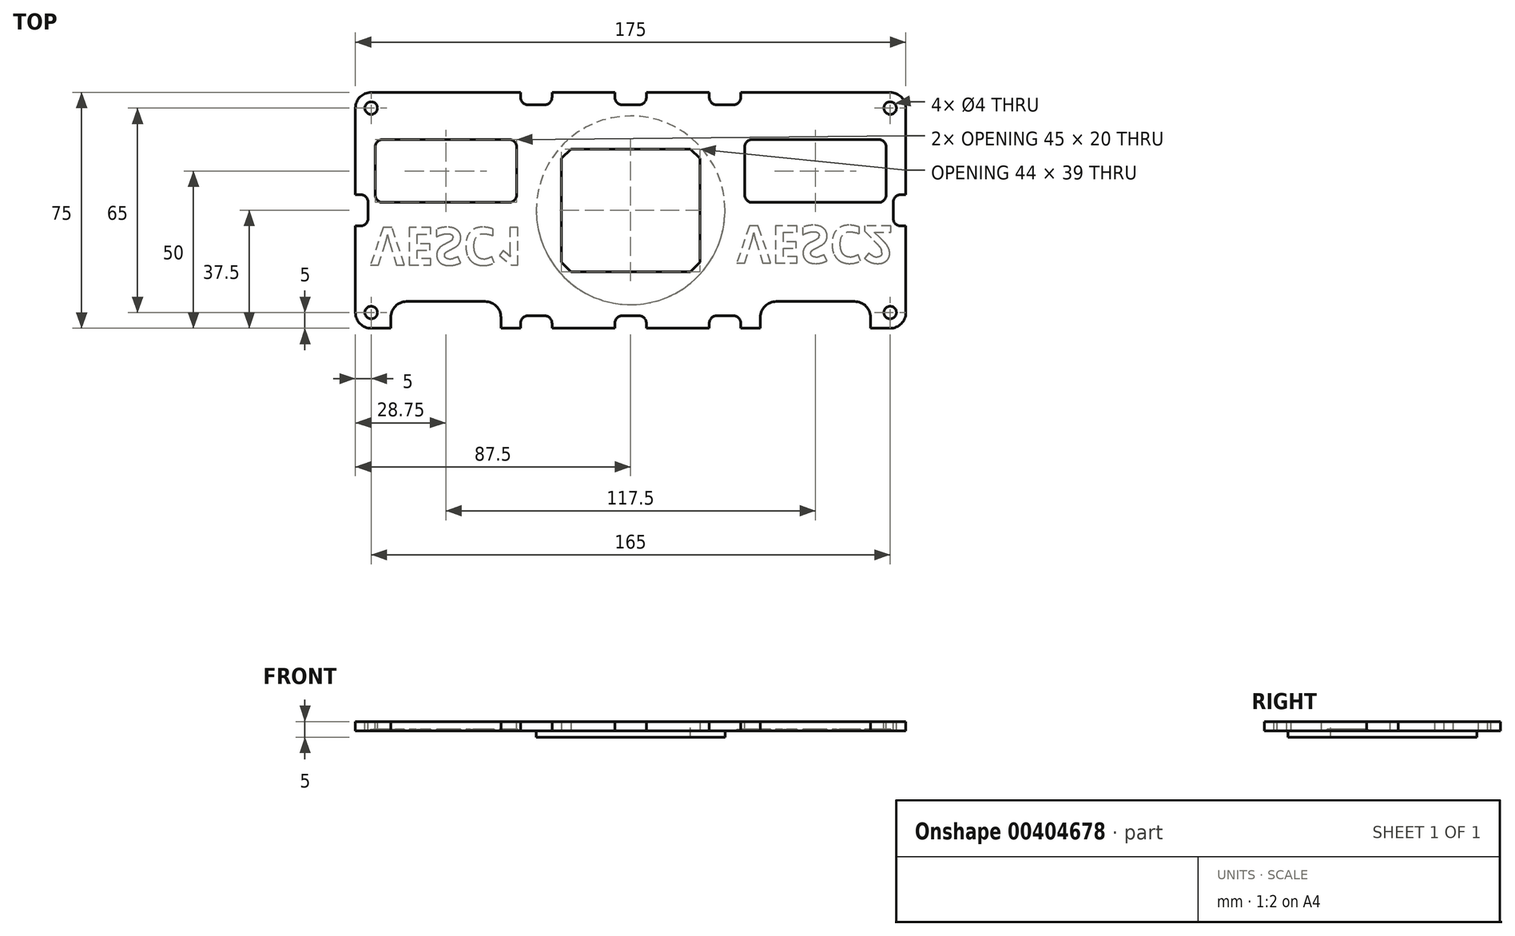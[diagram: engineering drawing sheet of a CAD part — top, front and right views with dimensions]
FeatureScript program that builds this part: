
annotation { "Feature Type Name" : "Feature", "Feature Type Description" : "" }
export const myFeature = defineFeature(function(context is Context, id is Id, definition is map)
    precondition{}
    {
        {
            var Q0;
            Q0=qCreatedBy(makeId("Top.planeOp"),FACE);
            var sketch = newSketch(context, id + "F0", { "sketchPlane" : qUnion([Q0])});
            skLineSegment(sketch, "E0.bottom", {"start": v(82.5, 37.5) * mm, "end": v(-82.5, 37.5) * mm});
            skLineSegment(sketch, "E0.top", {"start": v(82.5, -37.5) * mm, "end": v(-82.5, -37.5) * mm});
            skLineSegment(sketch, "E0.left", {"start": v(87.5, 32.5) * mm, "end": v(87.5, -32.5) * mm});
            skLineSegment(sketch, "E0.right", {"start": v(-87.5, 32.5) * mm, "end": v(-87.5, -32.5) * mm});
            skPoint(sketch, "E0.middle", {"position": v(0, 0) * mm});
            skPoint(sketch, "E1.visualSharp", {"position": v(-87.5, 37.5) * mm});
            skArc(sketch, "E1.filletArc", {"start": v(-82.5, 37.5) * mm, "mid": v(-86.04, 36.04) * mm, "end": v(-87.5, 32.5) * mm});
            skPoint(sketch, "E2.visualSharp", {"position": v(87.5, 37.5) * mm});
            skArc(sketch, "E2.filletArc", {"start": v(87.5, 32.5) * mm, "mid": v(86.04, 36.04) * mm, "end": v(82.5, 37.5) * mm});
            skPoint(sketch, "E3.visualSharp", {"position": v(87.5, -37.5) * mm});
            skArc(sketch, "E3.filletArc", {"start": v(82.5, -37.5) * mm, "mid": v(86.04, -36.04) * mm, "end": v(87.5, -32.5) * mm});
            skPoint(sketch, "E4.visualSharp", {"position": v(-87.5, -37.5) * mm});
            skArc(sketch, "E4.filletArc", {"start": v(-87.5, -32.5) * mm, "mid": v(-86.04, -36.04) * mm, "end": v(-82.5, -37.5) * mm});
            skSolve(sketch);
        }
        {
            var Q0;
            Q0=makeQuery(id+"F0.imprint","IMPRINT",FACE,{"disambiguationData":[TD([[makeQuery(id+"F0.imprint","IMPRINT",EDGE,{"derivedFrom":sQuery(id+"F0.wireOp",EDGE,"E0.bottom")}),1.0]])]});
            extrude(context, id + "F1", {"entities" : qUnion([Q0]), "depth" : 3 * mm});
        }
        {
            var Q0;
            Q0=makeQuery(id+"F1.opExtrude","CAP_FACE",FACE,{"disambiguationData":[OSD([sQuery(id+"F0.wireOp",EDGE,"E0.bottom"),sQuery(id+"F0.wireOp",EDGE,"E0.top"),sQuery(id+"F0.wireOp",EDGE,"E0.left"),sQuery(id+"F0.wireOp",EDGE,"E0.right"),sQuery(id+"F0.wireOp",EDGE,"E1.filletArc"),sQuery(id+"F0.wireOp",EDGE,"E2.filletArc"),sQuery(id+"F0.wireOp",EDGE,"E3.filletArc"),sQuery(id+"F0.wireOp",EDGE,"E4.filletArc")])],"isStart":false});
            var sketch = newSketch(context, id + "F2", { "sketchPlane" : qUnion([Q0])});
            skLineSegment(sketch, "E5.bottom", {"start": v(35, 41.5) * mm, "end": v(-35, 41.5) * mm});
            skLineSegment(sketch, "E5.top", {"start": v(35, 33.5) * mm, "end": v(-35, 33.5) * mm});
            skLineSegment(sketch, "E5.left", {"start": v(35, 41.5) * mm, "end": v(35, 33.5) * mm});
            skLineSegment(sketch, "E5.right", {"start": v(-35, 41.5) * mm, "end": v(-35, 33.5) * mm});
            skPoint(sketch, "E5.middle", {"position": v(0, 37.5) * mm});
            skLineSegment(sketch, "E6.bottom", {"start": v(35, -41.5) * mm, "end": v(-35, -41.5) * mm});
            skLineSegment(sketch, "E6.top", {"start": v(35, -33.5) * mm, "end": v(-35, -33.5) * mm});
            skLineSegment(sketch, "E6.left", {"start": v(35, -41.5) * mm, "end": v(35, -33.5) * mm});
            skLineSegment(sketch, "E6.right", {"start": v(-35, -41.5) * mm, "end": v(-35, -33.5) * mm});
            skPoint(sketch, "E6.middle", {"position": v(0, -37.5) * mm});
            skLineSegment(sketch, "E7.bottom", {"start": v(-91.5, -5) * mm, "end": v(-83.5, -5) * mm});
            skLineSegment(sketch, "E7.top", {"start": v(-91.5, 5) * mm, "end": v(-83.5, 5) * mm});
            skLineSegment(sketch, "E7.left", {"start": v(-91.5, -5) * mm, "end": v(-91.5, 5) * mm});
            skLineSegment(sketch, "E7.right", {"start": v(-83.5, -5) * mm, "end": v(-83.5, 5) * mm});
            skPoint(sketch, "E7.middle", {"position": v(-87.5, 0) * mm});
            skLineSegment(sketch, "E8.bottom", {"start": v(91.5, -5) * mm, "end": v(83.5, -5) * mm});
            skLineSegment(sketch, "E8.top", {"start": v(91.5, 5) * mm, "end": v(83.5, 5) * mm});
            skLineSegment(sketch, "E8.left", {"start": v(91.5, -5) * mm, "end": v(91.5, 5) * mm});
            skLineSegment(sketch, "E8.right", {"start": v(83.5, -5) * mm, "end": v(83.5, 5) * mm});
            skPoint(sketch, "E8.middle", {"position": v(87.5, 0) * mm});
            skSolve(sketch);
        }
        {
            var Q0;
            {var subQ0=sQuery(id+"F2.wireOp",EDGE,"E7.right");Q0=makeQuery(id+"F2.imprint","IMPRINT",FACE,{"disambiguationData":[TD([[makeQuery(id+"F2.imprint","IMPRINT",EDGE,{"derivedFrom":subQ0}),1.0]])]});}
            var Q1;
            {var subQ0=sQuery(id+"F2.wireOp",EDGE,"E7.left");Q1=makeQuery(id+"F2.imprint","IMPRINT",FACE,{"disambiguationData":[TD([[makeQuery(id+"F2.imprint","IMPRINT",EDGE,{"derivedFrom":subQ0}),-1.0]])]});}
            var Q2;
            {var subQ0=sQuery(id+"F2.wireOp",EDGE,"E5.top");Q2=makeQuery(id+"F2.imprint","IMPRINT",FACE,{"disambiguationData":[TD([[makeQuery(id+"F2.imprint","IMPRINT",EDGE,{"derivedFrom":subQ0}),-1.0]])]});}
            var Q3;
            {var subQ0=sQuery(id+"F2.wireOp",EDGE,"E5.bottom");Q3=makeQuery(id+"F2.imprint","IMPRINT",FACE,{"disambiguationData":[TD([[makeQuery(id+"F2.imprint","IMPRINT",EDGE,{"derivedFrom":subQ0}),1.0]])]});}
            var Q4;
            {var subQ0=sQuery(id+"F2.wireOp",EDGE,"E8.right");Q4=makeQuery(id+"F2.imprint","IMPRINT",FACE,{"disambiguationData":[TD([[makeQuery(id+"F2.imprint","IMPRINT",EDGE,{"derivedFrom":subQ0}),-1.0]])]});}
            var Q5;
            {var subQ0=sQuery(id+"F2.wireOp",EDGE,"E8.left");Q5=makeQuery(id+"F2.imprint","IMPRINT",FACE,{"disambiguationData":[TD([[makeQuery(id+"F2.imprint","IMPRINT",EDGE,{"derivedFrom":subQ0}),1.0]])]});}
            var Q6;
            {var subQ0=sQuery(id+"F2.wireOp",EDGE,"E6.top");Q6=makeQuery(id+"F2.imprint","IMPRINT",FACE,{"disambiguationData":[TD([[makeQuery(id+"F2.imprint","IMPRINT",EDGE,{"derivedFrom":subQ0}),1.0]])]});}
            var Q7;
            {var subQ0=sQuery(id+"F2.wireOp",EDGE,"E6.bottom");Q7=makeQuery(id+"F2.imprint","IMPRINT",FACE,{"disambiguationData":[TD([[makeQuery(id+"F2.imprint","IMPRINT",EDGE,{"derivedFrom":subQ0}),-1.0]])]});}
            extrude(context, id + "F3", {"entities" : qUnion([Q0, Q1, Q2, Q3, Q4, Q5, Q6, Q7]), "operationType" : NewBodyOperationType.REMOVE, "oppositeDirection" : true, "depth" : 20.4 * mm});
        }
        {
            var Q0;
            Q0=makeQuery(id+"F1.opExtrude","CAP_FACE",FACE,{"disambiguationData":[OSD([sQuery(id+"F0.wireOp",EDGE,"E0.bottom"),sQuery(id+"F0.wireOp",EDGE,"E0.top"),sQuery(id+"F0.wireOp",EDGE,"E0.left"),sQuery(id+"F0.wireOp",EDGE,"E0.right"),sQuery(id+"F0.wireOp",EDGE,"E1.filletArc"),sQuery(id+"F0.wireOp",EDGE,"E2.filletArc"),sQuery(id+"F0.wireOp",EDGE,"E3.filletArc"),sQuery(id+"F0.wireOp",EDGE,"E4.filletArc")])],"isStart":false});
            var sketch = newSketch(context, id + "F4", { "sketchPlane" : qUnion([Q0])});
            skCircle(sketch, "E9", {"center": v(-82.5, 32.5) * mm, "radius": 2 * mm});
            skCircle(sketch, "E10", {"center": v(82.5, 32.5) * mm, "radius": 2 * mm});
            skCircle(sketch, "E11", {"center": v(-82.5, -32.5) * mm, "radius": 2 * mm});
            skCircle(sketch, "E12", {"center": v(82.5, -32.5) * mm, "radius": 2 * mm});
            skSolve(sketch);
        }
        {
            var Q0;
            Q0=makeQuery(id+"F4.imprint","IMPRINT",FACE,{"disambiguationData":[TD([[makeQuery(id+"F4.imprint","IMPRINT",EDGE,{"derivedFrom":sQuery(id+"F4.wireOp",EDGE,"E9")}),1.0]])]});
            var Q1;
            Q1=makeQuery(id+"F4.imprint","IMPRINT",FACE,{"disambiguationData":[TD([[makeQuery(id+"F4.imprint","IMPRINT",EDGE,{"derivedFrom":sQuery(id+"F4.wireOp",EDGE,"E11")}),1.0]])]});
            var Q2;
            Q2=makeQuery(id+"F4.imprint","IMPRINT",FACE,{"disambiguationData":[TD([[makeQuery(id+"F4.imprint","IMPRINT",EDGE,{"derivedFrom":sQuery(id+"F4.wireOp",EDGE,"E10")}),1.0]])]});
            var Q3;
            Q3=makeQuery(id+"F4.imprint","IMPRINT",FACE,{"disambiguationData":[TD([[makeQuery(id+"F4.imprint","IMPRINT",EDGE,{"derivedFrom":sQuery(id+"F4.wireOp",EDGE,"E12")}),1.0]])]});
            extrude(context, id + "F5", {"entities" : qUnion([Q0, Q1, Q2, Q3]), "operationType" : NewBodyOperationType.REMOVE, "oppositeDirection" : true, "depth" : 25 * mm});
        }
        {
            var Q0;
            Q0=makeQuery(id+"F1.opExtrude","CAP_FACE",FACE,{"disambiguationData":[OSD([sQuery(id+"F0.wireOp",EDGE,"E0.bottom"),sQuery(id+"F0.wireOp",EDGE,"E0.top"),sQuery(id+"F0.wireOp",EDGE,"E0.left"),sQuery(id+"F0.wireOp",EDGE,"E0.right"),sQuery(id+"F0.wireOp",EDGE,"E1.filletArc"),sQuery(id+"F0.wireOp",EDGE,"E2.filletArc"),sQuery(id+"F0.wireOp",EDGE,"E3.filletArc"),sQuery(id+"F0.wireOp",EDGE,"E4.filletArc")])],"isStart":false});
            var sketch = newSketch(context, id + "F6", { "sketchPlane" : qUnion([Q0])});
            skLineSegment(sketch, "E13.bottom", {"start": v(22, 19.5) * mm, "end": v(-22, 19.5) * mm});
            skLineSegment(sketch, "E13.top", {"start": v(22, -19.5) * mm, "end": v(-22, -19.5) * mm});
            skLineSegment(sketch, "E13.left", {"start": v(22, 19.5) * mm, "end": v(22, -19.5) * mm});
            skLineSegment(sketch, "E13.right", {"start": v(-22, 19.5) * mm, "end": v(-22, -19.5) * mm});
            skPoint(sketch, "E13.middle", {"position": v(0, 0) * mm});
            skSolve(sketch);
        }
        {
            var Q0;
            Q0=makeQuery(id+"F6.imprint","IMPRINT",FACE,{"disambiguationData":[TD([[makeQuery(id+"F6.imprint","IMPRINT",EDGE,{"derivedFrom":sQuery(id+"F6.wireOp",EDGE,"E13.bottom")}),1.0]])]});
            extrude(context, id + "F7", {"entities" : qUnion([Q0]), "operationType" : NewBodyOperationType.REMOVE, "oppositeDirection" : true, "depth" : 25 * mm});
        }
        {
            var Q0;
            Q0=makeQuery(id+"F1.opExtrude","CAP_FACE",FACE,{"disambiguationData":[OSD([sQuery(id+"F0.wireOp",EDGE,"E0.bottom"),sQuery(id+"F0.wireOp",EDGE,"E0.top"),sQuery(id+"F0.wireOp",EDGE,"E0.left"),sQuery(id+"F0.wireOp",EDGE,"E0.right"),sQuery(id+"F0.wireOp",EDGE,"E1.filletArc"),sQuery(id+"F0.wireOp",EDGE,"E2.filletArc"),sQuery(id+"F0.wireOp",EDGE,"E3.filletArc"),sQuery(id+"F0.wireOp",EDGE,"E4.filletArc")])],"isStart":false});
            var sketch = newSketch(context, id + "F8", { "sketchPlane" : qUnion([Q0])});
            skLineSegment(sketch, "E14.bottom", {"start": v(-41.25, -46) * mm, "end": v(-76.25, -46) * mm});
            skLineSegment(sketch, "E14.top", {"start": v(-46.25, -29) * mm, "end": v(-71.25, -29) * mm});
            skLineSegment(sketch, "E14.left", {"start": v(-41.25, -46) * mm, "end": v(-41.25, -34) * mm});
            skLineSegment(sketch, "E14.right", {"start": v(-76.25, -46) * mm, "end": v(-76.25, -34) * mm});
            skPoint(sketch, "E14.middle", {"position": v(-58.75, -37.5) * mm});
            skPoint(sketch, "E15.visualSharp", {"position": v(-76.25, -29) * mm});
            skArc(sketch, "E15.filletArc", {"start": v(-71.25, -29) * mm, "mid": v(-74.79, -30.46) * mm, "end": v(-76.25, -34) * mm});
            skPoint(sketch, "E16.visualSharp", {"position": v(-41.25, -29) * mm});
            skArc(sketch, "E16.filletArc", {"start": v(-41.25, -34) * mm, "mid": v(-42.71, -30.46) * mm, "end": v(-46.25, -29) * mm});
            skLineSegment(sketch, "E17.bottom", {"start": v(76.25, -46) * mm, "end": v(41.25, -46) * mm});
            skLineSegment(sketch, "E17.top", {"start": v(71.25, -29) * mm, "end": v(46.25, -29) * mm});
            skLineSegment(sketch, "E17.left", {"start": v(76.25, -46) * mm, "end": v(76.25, -34) * mm});
            skLineSegment(sketch, "E17.right", {"start": v(41.25, -46) * mm, "end": v(41.25, -34) * mm});
            skPoint(sketch, "E17.middle", {"position": v(58.75, -37.5) * mm});
            skPoint(sketch, "E18.visualSharp", {"position": v(41.25, -29) * mm});
            skArc(sketch, "E18.filletArc", {"start": v(46.25, -29) * mm, "mid": v(42.71, -30.46) * mm, "end": v(41.25, -34) * mm});
            skPoint(sketch, "E19.visualSharp", {"position": v(76.25, -29) * mm});
            skArc(sketch, "E19.filletArc", {"start": v(76.25, -34) * mm, "mid": v(74.79, -30.46) * mm, "end": v(71.25, -29) * mm});
            skSolve(sketch);
        }
        {
            var Q0;
            Q0 = qSketchRegion(id + "F8", true);
            extrude(context, id + "F9", {"entities" : qUnion([Q0]), "operationType" : NewBodyOperationType.REMOVE, "oppositeDirection" : true, "depth" : 25 * mm});
        }
        {
            var Q0;
            Q0=makeQuery(id+"F1.opExtrude","CAP_FACE",FACE,{"disambiguationData":[OSD([sQuery(id+"F0.wireOp",EDGE,"E0.bottom"),sQuery(id+"F0.wireOp",EDGE,"E0.top"),sQuery(id+"F0.wireOp",EDGE,"E0.left"),sQuery(id+"F0.wireOp",EDGE,"E0.right"),sQuery(id+"F0.wireOp",EDGE,"E1.filletArc"),sQuery(id+"F0.wireOp",EDGE,"E2.filletArc"),sQuery(id+"F0.wireOp",EDGE,"E3.filletArc"),sQuery(id+"F0.wireOp",EDGE,"E4.filletArc")])],"isStart":false});
            var sketch = newSketch(context, id + "F10", { "sketchPlane" : qUnion([Q0])});
            skLineSegment(sketch, "E20.bottom", {"start": v(5, -37.5) * mm, "end": v(-5, -37.5) * mm});
            skLineSegment(sketch, "E20.top", {"start": v(5, -29.5) * mm, "end": v(-5, -29.5) * mm});
            skLineSegment(sketch, "E20.left", {"start": v(5, -37.5) * mm, "end": v(5, -29.5) * mm});
            skLineSegment(sketch, "E20.right", {"start": v(-5, -37.5) * mm, "end": v(-5, -29.5) * mm});
            skPoint(sketch, "E20.middle", {"position": v(0, -33.5) * mm});
            skLineSegment(sketch, "E21.bottom", {"start": v(-5, -37.5) * mm, "end": v(-25, -37.5) * mm});
            skLineSegment(sketch, "E21.top", {"start": v(-5, -29.5) * mm, "end": v(-25, -29.5) * mm});
            skLineSegment(sketch, "E21.right", {"start": v(-25, -37.5) * mm, "end": v(-25, -29.5) * mm});
            skPoint(sketch, "E21.middle", {"position": v(-15, -33.5) * mm});
            skLineSegment(sketch, "E22.bottom", {"start": v(5, -37.5) * mm, "end": v(25, -37.5) * mm});
            skLineSegment(sketch, "E22.top", {"start": v(5, -29.5) * mm, "end": v(25, -29.5) * mm});
            skLineSegment(sketch, "E22.right", {"start": v(25, -37.5) * mm, "end": v(25, -29.5) * mm});
            skPoint(sketch, "E22.middle", {"position": v(15, -33.5) * mm});
            skLineSegment(sketch, "E23", {"start": v(-98.16, 0) * mm, "end": v(103.56, 0) * mm});
            skLineSegment(sketch, "E24.MirrorCS", {"start": v(-5, 37.5) * mm, "end": v(-25, 37.5) * mm});
            skLineSegment(sketch, "E25.MirrorCS", {"start": v(-25, 37.5) * mm, "end": v(-25, 29.5) * mm});
            skLineSegment(sketch, "E26.MirrorCS", {"start": v(-5, 29.5) * mm, "end": v(-25, 29.5) * mm});
            skLineSegment(sketch, "E27.MirrorCS", {"start": v(-5, 37.5) * mm, "end": v(-5, 29.5) * mm});
            skLineSegment(sketch, "E28.MirrorCS", {"start": v(5, 37.5) * mm, "end": v(5, 29.5) * mm});
            skLineSegment(sketch, "E29.MirrorCS", {"start": v(5, 29.5) * mm, "end": v(25, 29.5) * mm});
            skLineSegment(sketch, "E30.MirrorCS", {"start": v(5, 37.5) * mm, "end": v(25, 37.5) * mm});
            skLineSegment(sketch, "E31.MirrorCS", {"start": v(25, 37.5) * mm, "end": v(25, 29.5) * mm});
            skSolve(sketch);
        }
        {
            var Q0;
            {var subQ0=sQuery(id+"F10.wireOp",EDGE,"E21.bottom");Q0=makeQuery(id+"F10.imprint","IMPRINT",FACE,{"disambiguationData":[TD([[makeQuery(id+"F10.imprint","IMPRINT",EDGE,{"derivedFrom":subQ0}),-1.0]])]});}
            var Q1;
            {var subQ0=sQuery(id+"F10.wireOp",EDGE,"E22.bottom");Q1=makeQuery(id+"F10.imprint","IMPRINT",FACE,{"disambiguationData":[TD([[makeQuery(id+"F10.imprint","IMPRINT",EDGE,{"derivedFrom":subQ0}),1.0]])]});}
            var Q2;
            {var subQ0=sQuery(id+"F10.wireOp",EDGE,"E21.top");Q2=makeQuery(id+"F10.imprint","IMPRINT",FACE,{"disambiguationData":[TD([[makeQuery(id+"F10.imprint","IMPRINT",EDGE,{"derivedFrom":subQ0}),1.0]])]});}
            var Q3;
            {var subQ0=sQuery(id+"F10.wireOp",EDGE,"E22.top");Q3=makeQuery(id+"F10.imprint","IMPRINT",FACE,{"disambiguationData":[TD([[makeQuery(id+"F10.imprint","IMPRINT",EDGE,{"derivedFrom":subQ0}),-1.0]])]});}
            var Q4;
            {var subQ0=sQuery(id+"F10.wireOp",EDGE,"E26.MirrorCS");Q4=makeQuery(id+"F10.imprint","IMPRINT",FACE,{"disambiguationData":[TD([[makeQuery(id+"F10.imprint","IMPRINT",EDGE,{"derivedFrom":subQ0}),-1.0]])]});}
            var Q5;
            {var subQ0=sQuery(id+"F10.wireOp",EDGE,"E24.MirrorCS");Q5=makeQuery(id+"F10.imprint","IMPRINT",FACE,{"disambiguationData":[TD([[makeQuery(id+"F10.imprint","IMPRINT",EDGE,{"derivedFrom":subQ0}),1.0]])]});}
            var Q6;
            {var subQ0=sQuery(id+"F10.wireOp",EDGE,"E30.MirrorCS");Q6=makeQuery(id+"F10.imprint","IMPRINT",FACE,{"disambiguationData":[TD([[makeQuery(id+"F10.imprint","IMPRINT",EDGE,{"derivedFrom":subQ0}),-1.0]])]});}
            var Q7;
            {var subQ0=sQuery(id+"F10.wireOp",EDGE,"E29.MirrorCS");Q7=makeQuery(id+"F10.imprint","IMPRINT",FACE,{"disambiguationData":[TD([[makeQuery(id+"F10.imprint","IMPRINT",EDGE,{"derivedFrom":subQ0}),1.0]])]});}
            extrude(context, id + "F11", {"entities" : qUnion([Q0, Q1, Q2, Q3, Q4, Q5, Q6, Q7]), "operationType" : NewBodyOperationType.ADD, "oppositeDirection" : true, "depth" : 3 * mm});
        }
        {
            var Q0;
            Q0=makeQuery(id+"F11.boolean.opBoolean","MERGE",FACE,{"derivedFrom":[makeQuery(id+"F1.opExtrude","CAP_FACE",FACE,{"disambiguationData":[OSD([sQuery(id+"F0.wireOp",EDGE,"E0.bottom"),sQuery(id+"F0.wireOp",EDGE,"E0.top"),sQuery(id+"F0.wireOp",EDGE,"E0.left"),sQuery(id+"F0.wireOp",EDGE,"E0.right"),sQuery(id+"F0.wireOp",EDGE,"E1.filletArc"),sQuery(id+"F0.wireOp",EDGE,"E2.filletArc"),sQuery(id+"F0.wireOp",EDGE,"E3.filletArc"),sQuery(id+"F0.wireOp",EDGE,"E4.filletArc")])],"isStart":false}),makeQuery(id+"F11.opExtrude","CAP_FACE",FACE,{"disambiguationData":[OSD([sQuery(id+"F10.wireOp",EDGE,"E21.bottom"),sQuery(id+"F10.wireOp",EDGE,"E21.top"),sQuery(id+"F10.wireOp",EDGE,"E20.right"),sQuery(id+"F10.wireOp",EDGE,"E21.right")])],"isStart":true}),makeQuery(id+"F11.opExtrude","CAP_FACE",FACE,{"disambiguationData":[OSD([sQuery(id+"F10.wireOp",EDGE,"E22.bottom"),sQuery(id+"F10.wireOp",EDGE,"E22.top"),sQuery(id+"F10.wireOp",EDGE,"E20.left"),sQuery(id+"F10.wireOp",EDGE,"E22.right")])],"isStart":true}),makeQuery(id+"F11.opExtrude","CAP_FACE",FACE,{"disambiguationData":[OSD([sQuery(id+"F10.wireOp",EDGE,"E24.MirrorCS"),sQuery(id+"F10.wireOp",EDGE,"E25.MirrorCS"),sQuery(id+"F10.wireOp",EDGE,"E26.MirrorCS"),sQuery(id+"F10.wireOp",EDGE,"E27.MirrorCS")])],"isStart":true}),makeQuery(id+"F11.opExtrude","CAP_FACE",FACE,{"disambiguationData":[OSD([sQuery(id+"F10.wireOp",EDGE,"E28.MirrorCS"),sQuery(id+"F10.wireOp",EDGE,"E29.MirrorCS"),sQuery(id+"F10.wireOp",EDGE,"E30.MirrorCS"),sQuery(id+"F10.wireOp",EDGE,"E31.MirrorCS")])],"isStart":true})]});
            var sketch = newSketch(context, id + "F12", { "sketchPlane" : qUnion([Q0])});
            skLineSegment(sketch, "E32.bottom", {"start": v(-81.25, 2.5) * mm, "end": v(-36.25, 2.5) * mm});
            skLineSegment(sketch, "E32.top", {"start": v(-81.25, 22.5) * mm, "end": v(-36.25, 22.5) * mm});
            skLineSegment(sketch, "E32.left", {"start": v(-81.25, 2.5) * mm, "end": v(-81.25, 22.5) * mm});
            skLineSegment(sketch, "E32.right", {"start": v(-36.25, 2.5) * mm, "end": v(-36.25, 22.5) * mm});
            skPoint(sketch, "E32.middle", {"position": v(-58.75, 12.5) * mm});
            skLineSegment(sketch, "E33", {"start": v(0, 66.3) * mm, "end": v(0, -42.19) * mm});
            skLineSegment(sketch, "E34.MirrorCS", {"start": v(81.25, 22.5) * mm, "end": v(36.25, 22.5) * mm});
            skLineSegment(sketch, "E35.MirrorCS", {"start": v(36.25, 2.5) * mm, "end": v(36.25, 22.5) * mm});
            skLineSegment(sketch, "E36.MirrorCS", {"start": v(81.25, 2.5) * mm, "end": v(36.25, 2.5) * mm});
            skLineSegment(sketch, "E37.MirrorCS", {"start": v(81.25, 2.5) * mm, "end": v(81.25, 22.5) * mm});
            skSolve(sketch);
        }
        {
            var Q0;
            {var subQ0=sQuery(id+"F12.wireOp",EDGE,"E32.right");Q0=makeQuery(id+"F12.imprint","IMPRINT",FACE,{"disambiguationData":[TD([[makeQuery(id+"F12.imprint","IMPRINT",EDGE,{"derivedFrom":subQ0}),1.0]])]});}
            var Q1;
            {var subQ0=sQuery(id+"F12.wireOp",EDGE,"E35.MirrorCS");Q1=makeQuery(id+"F12.imprint","IMPRINT",FACE,{"disambiguationData":[TD([[makeQuery(id+"F12.imprint","IMPRINT",EDGE,{"derivedFrom":subQ0}),-1.0]])]});}
            extrude(context, id + "F13", {"entities" : qUnion([Q0, Q1]), "operationType" : NewBodyOperationType.REMOVE, "oppositeDirection" : true, "depth" : 25 * mm});
        }
        {
            var Q0;
            Q0=makeQuery(id+"F13.boolean.opBoolean","COPY",EDGE,{"derivedFrom":makeQuery(id+"F13.opExtrude","SWEPT_EDGE",EDGE,{"disambiguationData":[OSD([sQuery(id+"F12.wireOp",EDGE,"E32.top"),sQuery(id+"F12.wireOp",EDGE,"E32.right")])]})});
            var Q1;
            Q1=makeQuery(id+"F13.boolean.opBoolean","COPY",EDGE,{"derivedFrom":makeQuery(id+"F13.opExtrude","SWEPT_EDGE",EDGE,{"disambiguationData":[OSD([sQuery(id+"F12.wireOp",EDGE,"E32.bottom"),sQuery(id+"F12.wireOp",EDGE,"E32.right")])]})});
            var Q2;
            Q2=makeQuery(id+"F11.boolean.opBoolean","INTERSECT",EDGE,{"derivedFrom":[makeQuery(id+"F3.boolean.opBoolean","COPY",FACE,{"derivedFrom":makeQuery(id+"F3.opExtrude","SWEPT_FACE",FACE,{"disambiguationData":[OSD([sQuery(id+"F2.wireOp",EDGE,"E5.top")])]})}),makeQuery(id+"F11.opExtrude","SWEPT_FACE",FACE,{"disambiguationData":[OSD([sQuery(id+"F10.wireOp",EDGE,"E25.MirrorCS")])]})]});
            var Q3;
            Q3=makeQuery(id+"F3.boolean.opBoolean","COPY",EDGE,{"derivedFrom":makeQuery(id+"F3.opExtrude","SWEPT_EDGE",EDGE,{"disambiguationData":[OSD([sQuery(id+"F2.wireOp",EDGE,"E5.top"),sQuery(id+"F2.wireOp",EDGE,"E5.right")])]})});
            var Q4;
            Q4=makeQuery(id+"F11.boolean.opBoolean","INTERSECT",EDGE,{"derivedFrom":[makeQuery(id+"F3.boolean.opBoolean","COPY",FACE,{"derivedFrom":makeQuery(id+"F3.opExtrude","SWEPT_FACE",FACE,{"disambiguationData":[OSD([sQuery(id+"F2.wireOp",EDGE,"E5.top")])]})}),makeQuery(id+"F11.opExtrude","SWEPT_FACE",FACE,{"disambiguationData":[OSD([sQuery(id+"F10.wireOp",EDGE,"E27.MirrorCS")])]})]});
            var Q5;
            Q5=makeQuery(id+"F11.boolean.opBoolean","INTERSECT",EDGE,{"derivedFrom":[makeQuery(id+"F3.boolean.opBoolean","COPY",FACE,{"derivedFrom":makeQuery(id+"F3.opExtrude","SWEPT_FACE",FACE,{"disambiguationData":[OSD([sQuery(id+"F2.wireOp",EDGE,"E5.top")])]})}),makeQuery(id+"F11.opExtrude","SWEPT_FACE",FACE,{"disambiguationData":[OSD([sQuery(id+"F10.wireOp",EDGE,"E28.MirrorCS")])]})]});
            var Q6;
            Q6=makeQuery(id+"F11.boolean.opBoolean","INTERSECT",EDGE,{"derivedFrom":[makeQuery(id+"F3.boolean.opBoolean","COPY",FACE,{"derivedFrom":makeQuery(id+"F3.opExtrude","SWEPT_FACE",FACE,{"disambiguationData":[OSD([sQuery(id+"F2.wireOp",EDGE,"E5.top")])]})}),makeQuery(id+"F11.opExtrude","SWEPT_FACE",FACE,{"disambiguationData":[OSD([sQuery(id+"F10.wireOp",EDGE,"E31.MirrorCS")])]})]});
            var Q7;
            Q7=makeQuery(id+"F3.boolean.opBoolean","COPY",EDGE,{"derivedFrom":makeQuery(id+"F3.opExtrude","SWEPT_EDGE",EDGE,{"disambiguationData":[OSD([sQuery(id+"F2.wireOp",EDGE,"E5.top"),sQuery(id+"F2.wireOp",EDGE,"E5.left")])]})});
            var Q8;
            Q8=makeQuery(id+"F13.boolean.opBoolean","COPY",EDGE,{"derivedFrom":makeQuery(id+"F13.opExtrude","SWEPT_EDGE",EDGE,{"disambiguationData":[OSD([sQuery(id+"F12.wireOp",EDGE,"E34.MirrorCS"),sQuery(id+"F12.wireOp",EDGE,"E35.MirrorCS")])]})});
            var Q9;
            Q9=makeQuery(id+"F13.boolean.opBoolean","COPY",EDGE,{"derivedFrom":makeQuery(id+"F13.opExtrude","SWEPT_EDGE",EDGE,{"disambiguationData":[OSD([sQuery(id+"F12.wireOp",EDGE,"E35.MirrorCS"),sQuery(id+"F12.wireOp",EDGE,"E36.MirrorCS")])]})});
            var Q10;
            Q10=makeQuery(id+"F3.boolean.opBoolean","COPY",EDGE,{"derivedFrom":makeQuery(id+"F3.opExtrude","SWEPT_EDGE",EDGE,{"disambiguationData":[OSD([sQuery(id+"F2.wireOp",EDGE,"E6.top"),sQuery(id+"F2.wireOp",EDGE,"E6.left")])]})});
            var Q11;
            Q11=makeQuery(id+"F11.boolean.opBoolean","INTERSECT",EDGE,{"derivedFrom":[makeQuery(id+"F3.boolean.opBoolean","COPY",FACE,{"derivedFrom":makeQuery(id+"F3.opExtrude","SWEPT_FACE",FACE,{"disambiguationData":[OSD([sQuery(id+"F2.wireOp",EDGE,"E6.top")])]})}),makeQuery(id+"F11.opExtrude","SWEPT_FACE",FACE,{"disambiguationData":[OSD([sQuery(id+"F10.wireOp",EDGE,"E22.right")])]})]});
            var Q12;
            Q12=makeQuery(id+"F11.boolean.opBoolean","INTERSECT",EDGE,{"derivedFrom":[makeQuery(id+"F3.boolean.opBoolean","COPY",FACE,{"derivedFrom":makeQuery(id+"F3.opExtrude","SWEPT_FACE",FACE,{"disambiguationData":[OSD([sQuery(id+"F2.wireOp",EDGE,"E6.top")])]})}),makeQuery(id+"F11.opExtrude","SWEPT_FACE",FACE,{"disambiguationData":[OSD([sQuery(id+"F10.wireOp",EDGE,"E20.right")])]})]});
            var Q13;
            Q13=makeQuery(id+"F11.boolean.opBoolean","INTERSECT",EDGE,{"derivedFrom":[makeQuery(id+"F3.boolean.opBoolean","COPY",FACE,{"derivedFrom":makeQuery(id+"F3.opExtrude","SWEPT_FACE",FACE,{"disambiguationData":[OSD([sQuery(id+"F2.wireOp",EDGE,"E6.top")])]})}),makeQuery(id+"F11.opExtrude","SWEPT_FACE",FACE,{"disambiguationData":[OSD([sQuery(id+"F10.wireOp",EDGE,"E20.left")])]})]});
            var Q14;
            Q14=makeQuery(id+"F11.boolean.opBoolean","INTERSECT",EDGE,{"derivedFrom":[makeQuery(id+"F3.boolean.opBoolean","COPY",FACE,{"derivedFrom":makeQuery(id+"F3.opExtrude","SWEPT_FACE",FACE,{"disambiguationData":[OSD([sQuery(id+"F2.wireOp",EDGE,"E6.top")])]})}),makeQuery(id+"F11.opExtrude","SWEPT_FACE",FACE,{"disambiguationData":[OSD([sQuery(id+"F10.wireOp",EDGE,"E21.right")])]})]});
            var Q15;
            Q15=makeQuery(id+"F3.boolean.opBoolean","COPY",EDGE,{"derivedFrom":makeQuery(id+"F3.opExtrude","SWEPT_EDGE",EDGE,{"disambiguationData":[OSD([sQuery(id+"F2.wireOp",EDGE,"E6.top"),sQuery(id+"F2.wireOp",EDGE,"E6.right")])]})});
            var Q16;
            Q16=makeQuery(id+"F3.boolean.opBoolean","COPY",EDGE,{"derivedFrom":makeQuery(id+"F3.opExtrude","SWEPT_EDGE",EDGE,{"disambiguationData":[OSD([sQuery(id+"F2.wireOp",EDGE,"E8.top"),sQuery(id+"F2.wireOp",EDGE,"E8.right")])]})});
            var Q17;
            Q17=makeQuery(id+"F3.boolean.opBoolean","COPY",EDGE,{"derivedFrom":makeQuery(id+"F3.opExtrude","SWEPT_EDGE",EDGE,{"disambiguationData":[OSD([sQuery(id+"F2.wireOp",EDGE,"E8.bottom"),sQuery(id+"F2.wireOp",EDGE,"E8.right")])]})});
            var Q18;
            Q18=makeQuery(id+"F3.boolean.opBoolean","COPY",EDGE,{"derivedFrom":makeQuery(id+"F3.opExtrude","SWEPT_EDGE",EDGE,{"disambiguationData":[OSD([sQuery(id+"F2.wireOp",EDGE,"E7.bottom"),sQuery(id+"F2.wireOp",EDGE,"E7.right")])]})});
            var Q19;
            Q19=makeQuery(id+"F3.boolean.opBoolean","COPY",EDGE,{"derivedFrom":makeQuery(id+"F3.opExtrude","SWEPT_EDGE",EDGE,{"disambiguationData":[OSD([sQuery(id+"F2.wireOp",EDGE,"E7.top"),sQuery(id+"F2.wireOp",EDGE,"E7.right")])]})});
            var Q20;
            Q20=makeQuery(id+"F13.boolean.opBoolean","COPY",EDGE,{"derivedFrom":makeQuery(id+"F13.opExtrude","SWEPT_EDGE",EDGE,{"disambiguationData":[OSD([sQuery(id+"F12.wireOp",EDGE,"E32.bottom"),sQuery(id+"F12.wireOp",EDGE,"E32.left")])]})});
            var Q21;
            Q21=makeQuery(id+"F13.boolean.opBoolean","COPY",EDGE,{"derivedFrom":makeQuery(id+"F13.opExtrude","SWEPT_EDGE",EDGE,{"disambiguationData":[OSD([sQuery(id+"F12.wireOp",EDGE,"E32.top"),sQuery(id+"F12.wireOp",EDGE,"E32.left")])]})});
            var Q22;
            Q22=makeQuery(id+"F13.boolean.opBoolean","COPY",EDGE,{"derivedFrom":makeQuery(id+"F13.opExtrude","SWEPT_EDGE",EDGE,{"disambiguationData":[OSD([sQuery(id+"F12.wireOp",EDGE,"E34.MirrorCS"),sQuery(id+"F12.wireOp",EDGE,"E37.MirrorCS")])]})});
            var Q23;
            Q23=makeQuery(id+"F13.boolean.opBoolean","COPY",EDGE,{"derivedFrom":makeQuery(id+"F13.opExtrude","SWEPT_EDGE",EDGE,{"disambiguationData":[OSD([sQuery(id+"F12.wireOp",EDGE,"E36.MirrorCS"),sQuery(id+"F12.wireOp",EDGE,"E37.MirrorCS")])]})});
            fillet(context, id + "F14", {"entities" : qUnion([Q0, Q1, Q2, Q3, Q4, Q5, Q6, Q7, Q8, Q9, Q10, Q11, Q12, Q13, Q14, Q15, Q16, Q17, Q18, Q19, Q20, Q21, Q22, Q23]), "radius" : 2.41 * mm, "tangentPropagation" : true, "allowEdgeOverflow" : false});
        }
        {
            var Q0;
            Q0=makeQuery(id+"F7.boolean.opBoolean","COPY",EDGE,{"derivedFrom":makeQuery(id+"F7.opExtrude","SWEPT_EDGE",EDGE,{"disambiguationData":[OSD([sQuery(id+"F6.wireOp",EDGE,"E13.bottom"),sQuery(id+"F6.wireOp",EDGE,"E13.right")])]})});
            var Q1;
            Q1=makeQuery(id+"F7.boolean.opBoolean","COPY",EDGE,{"derivedFrom":makeQuery(id+"F7.opExtrude","SWEPT_EDGE",EDGE,{"disambiguationData":[OSD([sQuery(id+"F6.wireOp",EDGE,"E13.bottom"),sQuery(id+"F6.wireOp",EDGE,"E13.left")])]})});
            var Q2;
            Q2=makeQuery(id+"F7.boolean.opBoolean","COPY",EDGE,{"derivedFrom":makeQuery(id+"F7.opExtrude","SWEPT_EDGE",EDGE,{"disambiguationData":[OSD([sQuery(id+"F6.wireOp",EDGE,"E13.top"),sQuery(id+"F6.wireOp",EDGE,"E13.right")])]})});
            var Q3;
            Q3=makeQuery(id+"F7.boolean.opBoolean","COPY",EDGE,{"derivedFrom":makeQuery(id+"F7.opExtrude","SWEPT_EDGE",EDGE,{"disambiguationData":[OSD([sQuery(id+"F6.wireOp",EDGE,"E13.top"),sQuery(id+"F6.wireOp",EDGE,"E13.left")])]})});
            chamfer(context, id + "F15", {"entities" : qUnion([Q0, Q1, Q2, Q3]), "width" : 3 * mm, "tangentPropagation" : true});
        }
        {
            var Q0;
            Q0=makeQuery(id+"F11.boolean.opBoolean","MERGE",FACE,{"derivedFrom":[makeQuery(id+"F1.opExtrude","CAP_FACE",FACE,{"disambiguationData":[OSD([sQuery(id+"F0.wireOp",EDGE,"E0.bottom"),sQuery(id+"F0.wireOp",EDGE,"E0.top"),sQuery(id+"F0.wireOp",EDGE,"E0.left"),sQuery(id+"F0.wireOp",EDGE,"E0.right"),sQuery(id+"F0.wireOp",EDGE,"E1.filletArc"),sQuery(id+"F0.wireOp",EDGE,"E2.filletArc"),sQuery(id+"F0.wireOp",EDGE,"E3.filletArc"),sQuery(id+"F0.wireOp",EDGE,"E4.filletArc")])],"isStart":true}),makeQuery(id+"F11.opExtrude","CAP_FACE",FACE,{"disambiguationData":[OSD([sQuery(id+"F10.wireOp",EDGE,"E21.bottom"),sQuery(id+"F10.wireOp",EDGE,"E21.top"),sQuery(id+"F10.wireOp",EDGE,"E20.right"),sQuery(id+"F10.wireOp",EDGE,"E21.right")])],"isStart":false}),makeQuery(id+"F11.opExtrude","CAP_FACE",FACE,{"disambiguationData":[OSD([sQuery(id+"F10.wireOp",EDGE,"E22.bottom"),sQuery(id+"F10.wireOp",EDGE,"E22.top"),sQuery(id+"F10.wireOp",EDGE,"E20.left"),sQuery(id+"F10.wireOp",EDGE,"E22.right")])],"isStart":false}),makeQuery(id+"F11.opExtrude","CAP_FACE",FACE,{"disambiguationData":[OSD([sQuery(id+"F10.wireOp",EDGE,"E24.MirrorCS"),sQuery(id+"F10.wireOp",EDGE,"E25.MirrorCS"),sQuery(id+"F10.wireOp",EDGE,"E26.MirrorCS"),sQuery(id+"F10.wireOp",EDGE,"E27.MirrorCS")])],"isStart":false}),makeQuery(id+"F11.opExtrude","CAP_FACE",FACE,{"disambiguationData":[OSD([sQuery(id+"F10.wireOp",EDGE,"E28.MirrorCS"),sQuery(id+"F10.wireOp",EDGE,"E29.MirrorCS"),sQuery(id+"F10.wireOp",EDGE,"E30.MirrorCS"),sQuery(id+"F10.wireOp",EDGE,"E31.MirrorCS")])],"isStart":false})]});
            var sketch = newSketch(context, id + "F16", { "sketchPlane" : qUnion([Q0])});
            skCircle(sketch, "E38", {"center": v(0, 0) * mm, "radius": 30 * mm});
            skSolve(sketch);
        }
        {
            var Q0;
            Q0=makeQuery(id+"F16.imprint","IMPRINT",FACE,{"disambiguationData":[TD([[makeQuery(id+"F16.imprint","IMPRINT",EDGE,{"derivedFrom":sQuery(id+"F16.wireOp",EDGE,"E38")}),1.0]])]});
            extrude(context, id + "F17", {"entities" : qUnion([Q0]), "operationType" : NewBodyOperationType.ADD, "depth" : 2 * mm});
        }
        {
            var Q0;
            Q0=makeQuery(id+"F11.boolean.opBoolean","MERGE",FACE,{"derivedFrom":[makeQuery(id+"F1.opExtrude","CAP_FACE",FACE,{"disambiguationData":[OSD([sQuery(id+"F0.wireOp",EDGE,"E0.bottom"),sQuery(id+"F0.wireOp",EDGE,"E0.top"),sQuery(id+"F0.wireOp",EDGE,"E0.left"),sQuery(id+"F0.wireOp",EDGE,"E0.right"),sQuery(id+"F0.wireOp",EDGE,"E1.filletArc"),sQuery(id+"F0.wireOp",EDGE,"E2.filletArc"),sQuery(id+"F0.wireOp",EDGE,"E3.filletArc"),sQuery(id+"F0.wireOp",EDGE,"E4.filletArc")])],"isStart":true}),makeQuery(id+"F11.opExtrude","CAP_FACE",FACE,{"disambiguationData":[OSD([sQuery(id+"F10.wireOp",EDGE,"E21.bottom"),sQuery(id+"F10.wireOp",EDGE,"E21.top"),sQuery(id+"F10.wireOp",EDGE,"E20.right"),sQuery(id+"F10.wireOp",EDGE,"E21.right")])],"isStart":false}),makeQuery(id+"F11.opExtrude","CAP_FACE",FACE,{"disambiguationData":[OSD([sQuery(id+"F10.wireOp",EDGE,"E22.bottom"),sQuery(id+"F10.wireOp",EDGE,"E22.top"),sQuery(id+"F10.wireOp",EDGE,"E20.left"),sQuery(id+"F10.wireOp",EDGE,"E22.right")])],"isStart":false}),makeQuery(id+"F11.opExtrude","CAP_FACE",FACE,{"disambiguationData":[OSD([sQuery(id+"F10.wireOp",EDGE,"E24.MirrorCS"),sQuery(id+"F10.wireOp",EDGE,"E25.MirrorCS"),sQuery(id+"F10.wireOp",EDGE,"E26.MirrorCS"),sQuery(id+"F10.wireOp",EDGE,"E27.MirrorCS")])],"isStart":false}),makeQuery(id+"F11.opExtrude","CAP_FACE",FACE,{"disambiguationData":[OSD([sQuery(id+"F10.wireOp",EDGE,"E28.MirrorCS"),sQuery(id+"F10.wireOp",EDGE,"E29.MirrorCS"),sQuery(id+"F10.wireOp",EDGE,"E30.MirrorCS"),sQuery(id+"F10.wireOp",EDGE,"E31.MirrorCS")])],"isStart":false})]});
            var sketch = newSketch(context, id + "F18", { "sketchPlane" : qUnion([Q0])});
            skText(sketch, "E39", { "text": "VESC1\n", "fontName": "OpenSans-Bold.ttf"});
            skText(sketch, "E40", { "text": "VESC2", "fontName": "OpenSans-Bold.ttf"});
            const initialGuessF18  = {"E39": [-0.08271, 0.0055, 1, 0, 0.012], "E40": [0.03374, 0.00488, 1, 0, 0.012]};
            skSetInitialGuess(sketch, initialGuessF18);
            skSolve(sketch);
        }
        {
            var Q0;
            Q0=makeQuery(id+"F18.imprint","IMPRINT",FACE,{"disambiguationData":[TD([[makeQuery(id+"F18.imprint","IMPRINT",EDGE,{"derivedFrom":sQuery(id+"F18.wireOp",EDGE,"E39.sketch_text.stroke-0")}),-1.0]])]});
            var Q1;
            Q1=makeQuery(id+"F18.imprint","IMPRINT",FACE,{"disambiguationData":[TD([[makeQuery(id+"F18.imprint","IMPRINT",EDGE,{"derivedFrom":sQuery(id+"F18.wireOp",EDGE,"E39.sketch_text.stroke-10")}),-1.0]])]});
            var Q2;
            Q2=makeQuery(id+"F18.imprint","IMPRINT",FACE,{"disambiguationData":[TD([[makeQuery(id+"F18.imprint","IMPRINT",EDGE,{"derivedFrom":sQuery(id+"F18.wireOp",EDGE,"E39.sketch_text.stroke-22")}),-1.0]])]});
            var Q3;
            Q3=makeQuery(id+"F18.imprint","IMPRINT",FACE,{"disambiguationData":[TD([[makeQuery(id+"F18.imprint","IMPRINT",EDGE,{"derivedFrom":sQuery(id+"F18.wireOp",EDGE,"E39.sketch_text.stroke-50")}),-1.0]])]});
            var Q4;
            Q4=makeQuery(id+"F18.imprint","IMPRINT",FACE,{"disambiguationData":[TD([[makeQuery(id+"F18.imprint","IMPRINT",EDGE,{"derivedFrom":sQuery(id+"F18.wireOp",EDGE,"E39.sketch_text.stroke-65")}),-1.0]])]});
            extrude(context, id + "F19", {"entities" : qUnion([Q0, Q1, Q2, Q3, Q4]), "operationType" : NewBodyOperationType.REMOVE, "oppositeDirection" : true, "depth" : 0.5 * mm});
        }
        {
            var Q0;
            Q0=makeQuery(id+"F18.imprint","IMPRINT",FACE,{"disambiguationData":[TD([[makeQuery(id+"F18.imprint","IMPRINT",EDGE,{"derivedFrom":sQuery(id+"F18.wireOp",EDGE,"E40.sketch_text.stroke-0")}),-1.0]])]});
            var Q1;
            Q1=makeQuery(id+"F18.imprint","IMPRINT",FACE,{"disambiguationData":[TD([[makeQuery(id+"F18.imprint","IMPRINT",EDGE,{"derivedFrom":sQuery(id+"F18.wireOp",EDGE,"E40.sketch_text.stroke-10")}),-1.0]])]});
            var Q2;
            Q2=makeQuery(id+"F18.imprint","IMPRINT",FACE,{"disambiguationData":[TD([[makeQuery(id+"F18.imprint","IMPRINT",EDGE,{"derivedFrom":sQuery(id+"F18.wireOp",EDGE,"E40.sketch_text.stroke-22")}),-1.0]])]});
            var Q3;
            Q3=makeQuery(id+"F18.imprint","IMPRINT",FACE,{"disambiguationData":[TD([[makeQuery(id+"F18.imprint","IMPRINT",EDGE,{"derivedFrom":sQuery(id+"F18.wireOp",EDGE,"E40.sketch_text.stroke-50")}),-1.0]])]});
            var Q4;
            Q4=makeQuery(id+"F18.imprint","IMPRINT",FACE,{"disambiguationData":[TD([[makeQuery(id+"F18.imprint","IMPRINT",EDGE,{"derivedFrom":sQuery(id+"F18.wireOp",EDGE,"E40.sketch_text.stroke-65")}),-1.0]])]});
            extrude(context, id + "F20", {"entities" : qUnion([Q0, Q1, Q2, Q3, Q4]), "operationType" : NewBodyOperationType.REMOVE, "oppositeDirection" : true, "depth" : 0.5 * mm});
        }
    });
